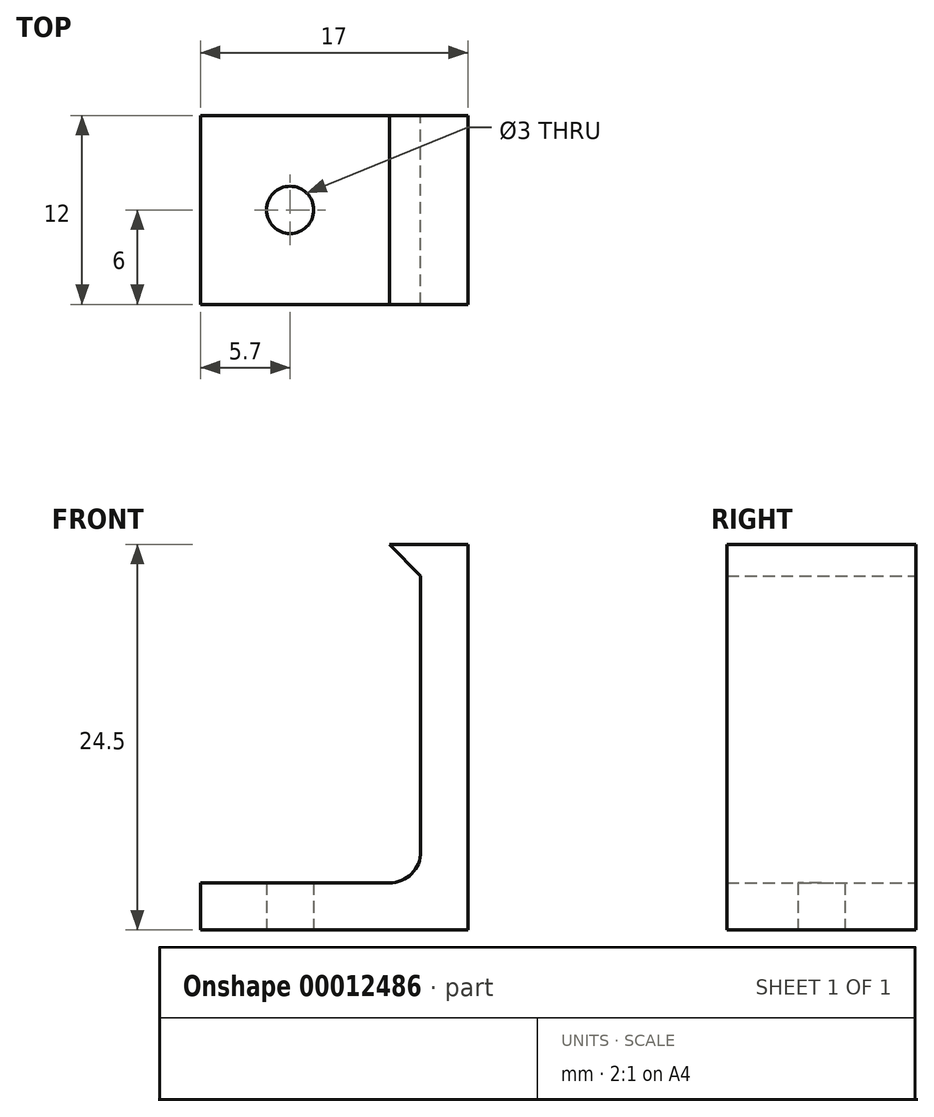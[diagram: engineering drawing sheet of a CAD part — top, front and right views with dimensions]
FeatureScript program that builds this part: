
annotation { "Feature Type Name" : "Feature", "Feature Type Description" : "" }
export const myFeature = defineFeature(function(context is Context, id is Id, definition is map)
    precondition{}
    {
        {
            var Q0;
            Q0=qCreatedBy(makeId("Front.planeOp"),FACE);
            var sketch = newSketch(context, id + "F0", { "sketchPlane" : qUnion([Q0])});
            skLineSegment(sketch, "E0", {"start": v(-17, 3) * mm, "end": v(-5, 3) * mm});
            skLineSegment(sketch, "E1", {"start": v(-3, 5) * mm, "end": v(-3, 22.5) * mm});
            skLineSegment(sketch, "E2", {"start": v(-3, 22.5) * mm, "end": v(0, 22.5) * mm});
            skLineSegment(sketch, "E3", {"start": v(0, 22.5) * mm, "end": v(0, 0) * mm});
            skLineSegment(sketch, "E4", {"start": v(0, 0) * mm, "end": v(-17, 0) * mm});
            skLineSegment(sketch, "E5", {"start": v(-17, 0) * mm, "end": v(-17, 3) * mm});
            skLineSegment(sketch, "E6", {"start": v(-3, 22.5) * mm, "end": v(-5, 24.5) * mm});
            skLineSegment(sketch, "E7", {"start": v(-5, 24.5) * mm, "end": v(0, 24.5) * mm});
            skLineSegment(sketch, "E8", {"start": v(0, 24.5) * mm, "end": v(0, 22.5) * mm});
            skPoint(sketch, "E9.visualSharp", {"position": v(-3, 3) * mm});
            skArc(sketch, "E9.filletArc", {"start": v(-5, 3) * mm, "mid": v(-3.59, 3.59) * mm, "end": v(-3, 5) * mm});
            skSolve(sketch);
        }
        {
            var Q0;
            Q0=qSketchRegion(id+"F0",true);
            extrude(context, id + "F1", {"entities" : qUnion([Q0]), "depth" : 12 * mm});
        }
        {
            var Q0;
            Q0=makeQuery(id+"F1.opExtrude","SWEPT_FACE",FACE,{"disambiguationData":[OSD([sQuery(id+"F0.wireOp",EDGE,"E4")])]});
            var sketch = newSketch(context, id + "F2", { "sketchPlane" : qUnion([Q0])});
            skCircle(sketch, "E10", {"center": v(-11.3, 6) * mm, "radius": 1.5 * mm});
            skSolve(sketch);
        }
        {
            var Q0;
            Q0=sQuery(id+"F2.wireOp",VERTEX,"E10.center");
            var Q1;
            Q1=makeQuery(id+"F1.opExtrude","SWEPT_BODY",BODY,{"disambiguationData":[OSD([sQuery(id+"F0.wireOp",EDGE,"E0"),sQuery(id+"F0.wireOp",EDGE,"E1"),sQuery(id+"F0.wireOp",EDGE,"E3"),sQuery(id+"F0.wireOp",EDGE,"E4"),sQuery(id+"F0.wireOp",EDGE,"E5"),sQuery(id+"F0.wireOp",EDGE,"E6"),sQuery(id+"F0.wireOp",EDGE,"E7"),sQuery(id+"F0.wireOp",EDGE,"E8")])]});
            hole(context, id + "F3", {"style" : HoleStyle.SIMPLE, "holeDiameter" : 3 * mm, "endStyle" : HoleEndStyle.BLIND, "holeDepth" : 20 * mm, "locations" : qUnion([Q0]), "scope" : qUnion([Q1])});
        }
    });
